# Revit family: Haworth_Pergola_Accessory_SpanningTop
name_source: partatom
category: Furniture Systems
revit_build: Autodesk Revit 2018 (Build: 20170223_1515(x64)
units: mm (PartAtom-declared; Revit-internal decimal feet)

## family parameters
Always vertical = Yes
Cut with Voids When Loaded = No
OmniClass Number = 23.40.70.14.64.21
OmniClass Title = Systems Furniture
Part Type = Normal
Room Calculation Point = No
Round Connector Dimension = Use Diameter
Shared = No
Work Plane-Based = No

## types (10) — shared parameters
Actual Height = 28"
Assembly Code = E2020200
Bracket Horizontal Offset = 8 1/4"
Description = Haworth - Pergola Spanning Top
Manufacturer = Haworth
Model = Haworth Pergola
Revision Number = 1
Size = Verify Final Dim. w/ Haworth
Standard Width = 48, 72, 96, 120, 144 in.
Sustainability Info = http://www.haworth.com
Trim Finish = Haworth _ Paint _ Undecided _ Pergola
URL = http://www.haworth.com
URL - Product = https://www.haworth.com
Warranty = http://www.haworth.com
Worksurface Finish = Haworth _ Laminate _ Undecided _ Pergola

## per-type parameters (varying)
- One-Sided - 48w: 120w=No; 144w=No; 48w=Yes; 72w=No; 96w=No; Actual Depth=14"; Actual Width=48"; Bracket Vertical Offset=4 1/2"; Bracket1-a=No; Bracket1-b=No; Bracket2-a=No; Bracket2-b=No; Bracket3-a=No; Bracket3-b=No; Bracket4-a=No; Bracket4-b=No; Bracket5-a=No; Bracket5-b=No; Bracket6-a=No; Bracket6-b=No; Bracket7-a=No; Bracket7-b=No; Half Depth=7"; Number of Brackets=0; One-Sided=Yes; Two-Sided=No; Width=48"
- One-Sided - 96w: 120w=No; 144w=No; 48w=No; 72w=No; 96w=Yes; Actual Depth=14"; Actual Width=96"; Bracket Vertical Offset=4 1/2"; Bracket1-a=No; Bracket1-b=No; Bracket2-a=Yes; Bracket2-b=No; Bracket3-a=No; Bracket3-b=No; Bracket4-a=No; Bracket4-b=No; Bracket5-a=No; Bracket5-b=No; Bracket6-a=Yes; Bracket6-b=No; Bracket7-a=No; Bracket7-b=No; Half Depth=7"; Number of Brackets=2; One-Sided=Yes; Two-Sided=No; Width=96"
- One-Sided - 120w: 120w=Yes; 144w=No; 48w=No; 72w=No; 96w=No; Actual Depth=14"; Actual Width=120"; Bracket Vertical Offset=4 1/2"; Bracket1-a=No; Bracket1-b=No; Bracket2-a=Yes; Bracket2-b=No; Bracket3-a=No; Bracket3-b=No; Bracket4-a=Yes; Bracket4-b=No; Bracket5-a=No; Bracket5-b=No; Bracket6-a=Yes; Bracket6-b=No; Bracket7-a=No; Bracket7-b=No; Half Depth=7"; Number of Brackets=3; One-Sided=Yes; Two-Sided=No; Width=120"
- Two-Sided - 120w: 120w=Yes; 144w=No; 48w=No; 72w=No; 96w=No; Actual Depth=21"; Actual Width=120"; Bracket Vertical Offset=3"; Bracket1-a=No; Bracket1-b=No; Bracket2-a=Yes; Bracket2-b=Yes; Bracket3-a=No; Bracket3-b=No; Bracket4-a=Yes; Bracket4-b=Yes; Bracket5-a=No; Bracket5-b=No; Bracket6-a=Yes; Bracket6-b=Yes; Bracket7-a=No; Bracket7-b=No; Half Depth=10 1/2"; Number of Brackets=3; One-Sided=No; Two-Sided=Yes; Width=120"
- Two-Sided - 96w: 120w=No; 144w=No; 48w=No; 72w=No; 96w=Yes; Actual Depth=21"; Actual Width=96"; Bracket Vertical Offset=3"; Bracket1-a=No; Bracket1-b=No; Bracket2-a=Yes; Bracket2-b=Yes; Bracket3-a=No; Bracket3-b=No; Bracket4-a=No; Bracket4-b=No; Bracket5-a=No; Bracket5-b=No; Bracket6-a=Yes; Bracket6-b=Yes; Bracket7-a=No; Bracket7-b=No; Half Depth=10 1/2"; Number of Brackets=2; One-Sided=No; Two-Sided=Yes; Width=96"
- Two-Sided - 72w: 120w=No; 144w=No; 48w=No; 72w=Yes; 96w=No; Actual Depth=21"; Actual Width=72"; Bracket Vertical Offset=3"; Bracket1-a=No; Bracket1-b=No; Bracket2-a=No; Bracket2-b=No; Bracket3-a=No; Bracket3-b=No; Bracket4-a=Yes; Bracket4-b=Yes; Bracket5-a=No; Bracket5-b=No; Bracket6-a=No; Bracket6-b=No; Bracket7-a=No; Bracket7-b=No; Half Depth=10 1/2"; Number of Brackets=1; One-Sided=No; Two-Sided=Yes; Width=72"
- Two-Sided - 48w: 120w=No; 144w=No; 48w=Yes; 72w=No; 96w=No; Actual Depth=21"; Actual Width=48"; Bracket Vertical Offset=3"; Bracket1-a=No; Bracket1-b=No; Bracket2-a=No; Bracket2-b=No; Bracket3-a=No; Bracket3-b=No; Bracket4-a=No; Bracket4-b=No; Bracket5-a=No; Bracket5-b=No; Bracket6-a=No; Bracket6-b=No; Bracket7-a=No; Bracket7-b=No; Half Depth=10 1/2"; Number of Brackets=0; One-Sided=No; Two-Sided=Yes; Width=48"
- Two-Sided - 144w: 120w=No; 144w=Yes; 48w=No; 72w=No; 96w=No; Actual Depth=21"; Actual Width=144"; Bracket Vertical Offset=3"; Bracket1-a=Yes; Bracket1-b=Yes; Bracket2-a=No; Bracket2-b=No; Bracket3-a=Yes; Bracket3-b=Yes; Bracket4-a=No; Bracket4-b=No; Bracket5-a=Yes; Bracket5-b=Yes; Bracket6-a=No; Bracket6-b=No; Bracket7-a=Yes; Bracket7-b=Yes; Half Depth=10 1/2"; Number of Brackets=4; One-Sided=No; Two-Sided=Yes; Width=144"
- One-Sided - 144w: 120w=No; 144w=Yes; 48w=No; 72w=No; 96w=No; Actual Depth=14"; Actual Width=144"; Bracket Vertical Offset=4 1/2"; Bracket1-a=Yes; Bracket1-b=No; Bracket2-a=No; Bracket2-b=No; Bracket3-a=Yes; Bracket3-b=No; Bracket4-a=No; Bracket4-b=No; Bracket5-a=Yes; Bracket5-b=No; Bracket6-a=No; Bracket6-b=No; Bracket7-a=Yes; Bracket7-b=No; Half Depth=7"; Number of Brackets=4; One-Sided=Yes; Two-Sided=No; Width=144"
- One-Sided - 72w: 120w=No; 144w=No; 48w=No; 72w=Yes; 96w=No; Actual Depth=14"; Actual Width=72"; Bracket Vertical Offset=4 1/2"; Bracket1-a=No; Bracket1-b=No; Bracket2-a=No; Bracket2-b=No; Bracket3-a=No; Bracket3-b=No; Bracket4-a=Yes; Bracket4-b=No; Bracket5-a=No; Bracket5-b=No; Bracket6-a=No; Bracket6-b=No; Bracket7-a=No; Bracket7-b=No; Half Depth=7"; Number of Brackets=1; One-Sided=Yes; Two-Sided=No; Width=72"

## geometry (parser evidence)
native form markers: Sweep x4
no freeform markers — native parametric forms only
